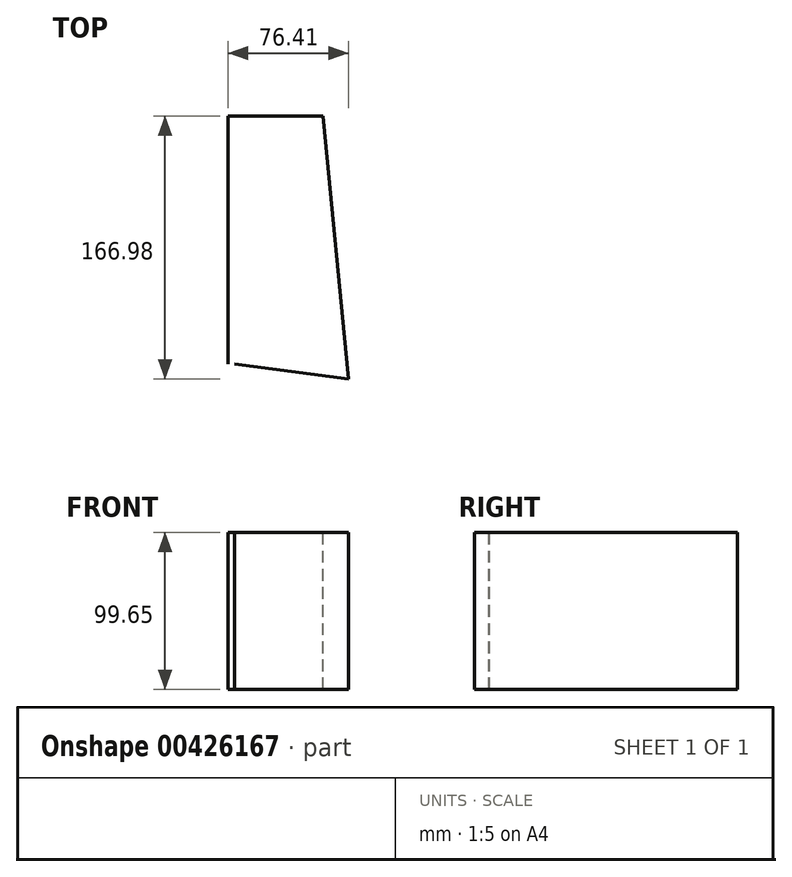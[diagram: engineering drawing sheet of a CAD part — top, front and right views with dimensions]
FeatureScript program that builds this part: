
annotation { "Feature Type Name" : "Feature", "Feature Type Description" : "" }
export const myFeature = defineFeature(function(context is Context, id is Id, definition is map)
    precondition{}
    {
        {
            var Q0;
            Q0=qCreatedBy(makeId("Top.planeOp"),FACE);
            var sketch = newSketch(context, id + "F0", { "sketchPlane" : qUnion([Q0])});
            skLineSegment(sketch, "E0", {"start": v(0, 0) * mm, "end": v(0, 157.33) * mm});
            skLineSegment(sketch, "E1", {"start": v(0, 157.33) * mm, "end": v(60.25, 157.33) * mm});
            skLineSegment(sketch, "E2", {"start": v(60.25, 157.33) * mm, "end": v(76.4, -9.65) * mm});
            skLineSegment(sketch, "E3", {"start": v(76.4, -9.65) * mm, "end": v(3.99, -0.26) * mm});
            skSolve(sketch);
        }
        {
            var Q0;
            Q0=sQuery(id+"F0.wireOp",EDGE,"E1");
            var Q1;
            Q1=sQuery(id+"F0.wireOp",EDGE,"E0");
            var Q2;
            Q2=sQuery(id+"F0.wireOp",EDGE,"E2");
            var Q3;
            Q3=sQuery(id+"F0.wireOp",EDGE,"E3");
            extrude(context, id + "F1", {"bodyType" : ToolBodyType.SURFACE, "surfaceEntities" : qUnion([Q0, Q1, Q2, Q3]), "depth" : 99.65 * mm});
        }
    });
